AUTODESK INVENTOR PART (.ipt)
format: ipt  version: 2021 (Build 250183000, 183)  size: 288,768 bytes
history: native  units: mm
features: extrude x3, other x2, fillet x2, chamfer x1, sketch x1
ambient origin geometry x8: Origin, YZ Plane, XZ Plane, XY Plane, X Axis, Y Axis, Z Axis, Center Point
bodies: Solid1 (feature_tree)
feature tree (9):
  extrude  "arm"  Depth=1.0mm
  other  "arm_holes_sketch"
  extrude  "arm_holes"  Depth=20.0mm
  fillet  "round_rot_edge"  Radius=10.0mm
  extrude  "Extrusion6"  Depth=1.0mm
  fillet  "Fillet4"  Radius=10.0mm
  chamfer  "Chamfer1"  Distance=4.0mm
  other  "arm_sketch"
  sketch  "Sketch6"  dims[d0=26.0mm d1=40.0mm d2=20.0mm d3=10.0mm d4=14.0mm d5=10.0mm d6=0.0mm d42=4.0mm d43=4.0mm d44=10.0mm d45=14.0mm d46=10.0mm d47=14.0mm d49=5.0mm d51=5.0mm d52=0.0mm d53=0.0mm d79=2.2mm d80=20.0mm d82=20.0mm d83=20.0mm d85=20.0mm d88=20.0mm d89=20.0mm d90=20.0mm d91=20.0mm d92=4.2mm d93=20.0mm d95=20.0mm d96=20.0mm d98=20.0mm d101=2.0mm d102=0.0mm d103=1.0mm d104=1.0mm d105=0.0mm d106=5.0mm d107=5.0mm d108=4.0mm d109=6.0mm d110=8.0mm d111=45.0deg]
